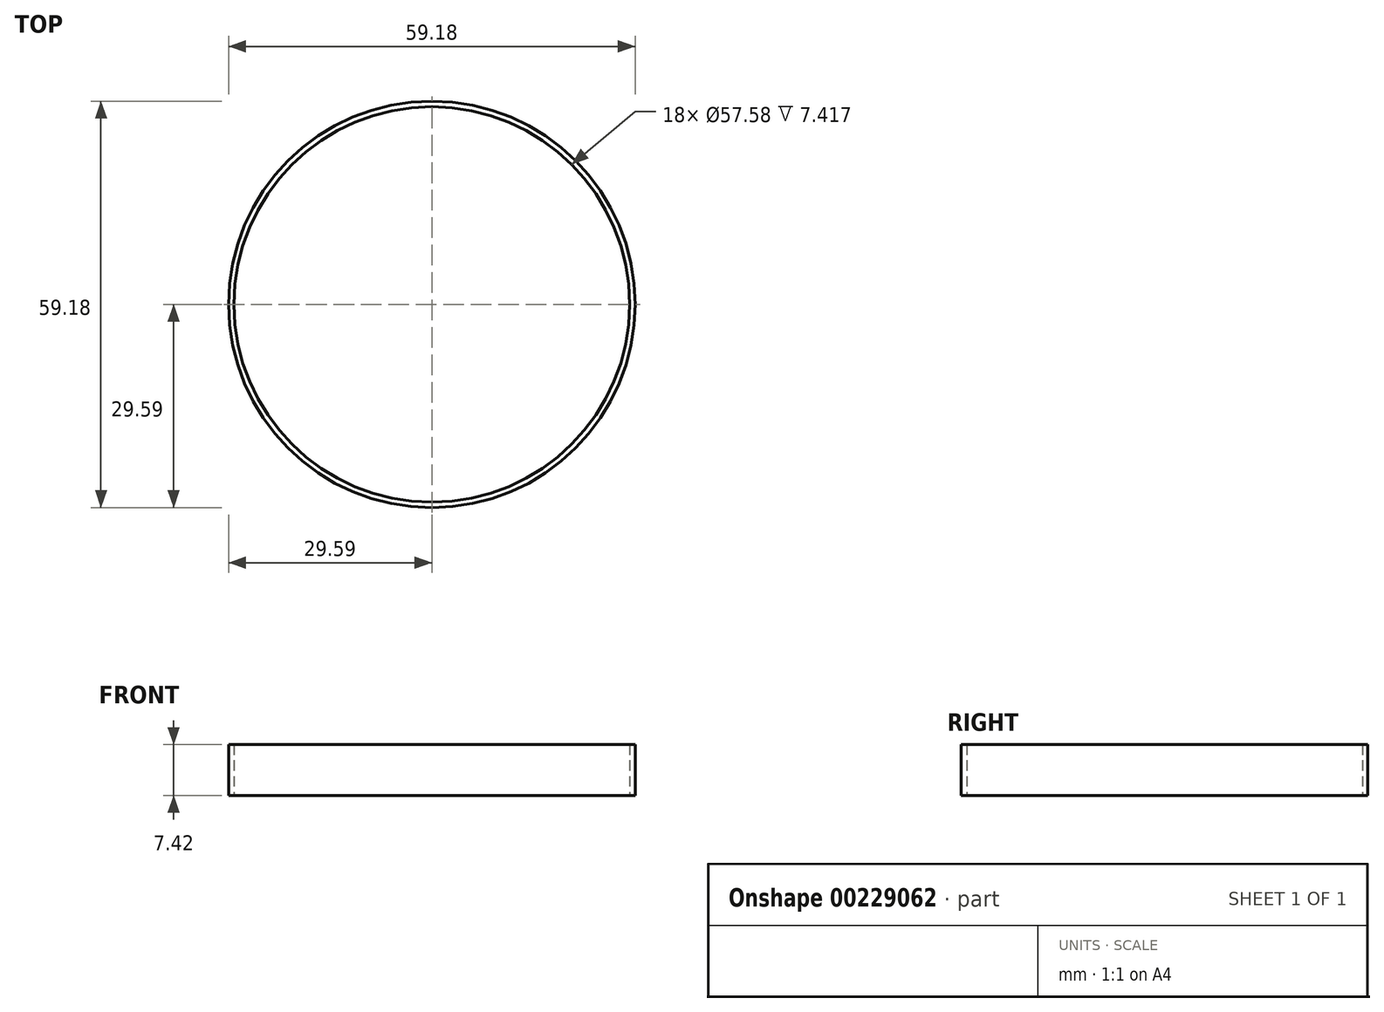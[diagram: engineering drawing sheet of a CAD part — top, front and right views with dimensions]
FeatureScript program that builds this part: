
annotation { "Feature Type Name" : "Feature", "Feature Type Description" : "" }
export const myFeature = defineFeature(function(context is Context, id is Id, definition is map)
    precondition{}
    {
        {
            var Q0;
            Q0=qCreatedBy(makeId("Top.planeOp"),FACE);
            var sketch = newSketch(context, id + "F0", { "sketchPlane" : qUnion([Q0])});
            skCircle(sketch, "E0", {"center": v(0, 0) * mm, "radius": 29.6 * mm});
            skSolve(sketch);
        }
        {
            var Q0;
            Q0 = qSketchRegion(id + "F0", true);
            extrude(context, id + "F1", {"entities" : qUnion([Q0]), "depth" : 7.42 * mm});
        }
        {
            var Q0;
            Q0=makeQuery(id+"F1.opExtrude","CAP_FACE",FACE,{"disambiguationData":[OSD([sQuery(id+"F0.wireOp",EDGE,"E0")])],"isStart":false});
            var Q1;
            Q1=makeQuery(id+"F1.opExtrude","CAP_FACE",FACE,{"disambiguationData":[OSD([sQuery(id+"F0.wireOp",EDGE,"E0")])],"isStart":true});
            shell(context, id + "F2", {"entities" : qUnion([Q0, Q1]), "thickness" : .8 * mm});
        }
    });
